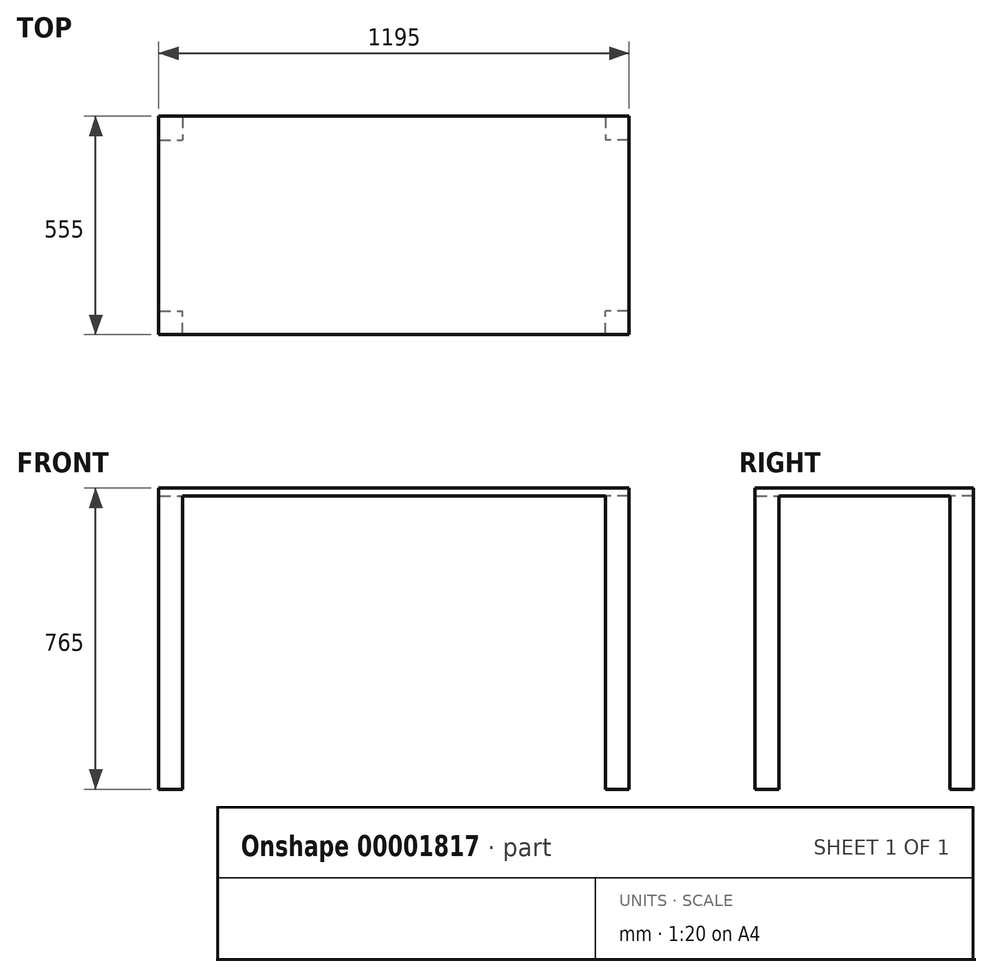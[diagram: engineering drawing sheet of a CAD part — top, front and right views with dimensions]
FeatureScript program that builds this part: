
annotation { "Feature Type Name" : "Feature", "Feature Type Description" : "" }
export const myFeature = defineFeature(function(context is Context, id is Id, definition is map)
    precondition{}
    {
        {
            var Q0;
            Q0=qCreatedBy(makeId("Top.planeOp"),FACE);
            var sketch = newSketch(context, id + "F0", { "sketchPlane" : qUnion([Q0])});
            skLineSegment(sketch, "E0.rect.bottom", {"start": v(597.5, -277.5) * mm, "end": v(-597.5, -277.5) * mm});
            skLineSegment(sketch, "E0.rect.top", {"start": v(597.5, 277.5) * mm, "end": v(-597.5, 277.5) * mm});
            skLineSegment(sketch, "E0.rect.left", {"start": v(597.5, -277.5) * mm, "end": v(597.5, 277.5) * mm});
            skLineSegment(sketch, "E0.rect.right", {"start": v(-597.5, -277.5) * mm, "end": v(-597.5, 277.5) * mm});
            skPoint(sketch, "E0.rect.middle", {"position": v(0, 0) * mm});
            skSolve(sketch);
        }
        {
            var Q0;
            Q0 = qSketchRegion(id + "F0", true);
            extrude(context, id + "F1", {"entities" : qUnion([Q0]), "depth" : 20 * mm});
        }
        {
            var Q0;
            Q0=makeQuery(id+"F1.opExtrude","CAP_FACE",FACE,{"disambiguationData":[OSD([sQuery(id+"F0.wireOp",EDGE,"E0.rect.bottom"),sQuery(id+"F0.wireOp",EDGE,"E0.rect.top"),sQuery(id+"F0.wireOp",EDGE,"E0.rect.left"),sQuery(id+"F0.wireOp",EDGE,"E0.rect.right")])],"isStart":true});
            var sketch = newSketch(context, id + "F2", { "sketchPlane" : qUnion([Q0])});
            skLineSegment(sketch, "E1", {"start": v(0, 277.5) * mm, "end": v(0, -277.5) * mm, "construction": true});
            skLineSegment(sketch, "E2.bottom", {"start": v(-597.5, 277.5) * mm, "end": v(-537.5, 277.5) * mm});
            skLineSegment(sketch, "E2.top", {"start": v(-597.5, 217.5) * mm, "end": v(-537.5, 217.5) * mm});
            skLineSegment(sketch, "E2.left", {"start": v(-597.5, 277.5) * mm, "end": v(-597.5, 217.5) * mm});
            skLineSegment(sketch, "E2.right", {"start": v(-537.5, 277.5) * mm, "end": v(-537.5, 217.5) * mm});
            skLineSegment(sketch, "E3.0.MirrorCS", {"start": v(597.5, 217.5) * mm, "end": v(537.5, 217.5) * mm});
            skLineSegment(sketch, "E4.0.MirrorCS", {"start": v(537.5, 277.5) * mm, "end": v(537.5, 217.5) * mm});
            skLineSegment(sketch, "E5.0.MirrorCS", {"start": v(597.5, 277.5) * mm, "end": v(537.5, 277.5) * mm});
            skLineSegment(sketch, "E6.2.MirrorCS", {"start": v(597.5, 277.5) * mm, "end": v(597.5, 217.5) * mm});
            skLineSegment(sketch, "E7", {"start": v(-597.5, 0) * mm, "end": v(597.5, 0) * mm, "construction": true});
            skLineSegment(sketch, "E8.0.MirrorCS", {"start": v(-597.5, -217.5) * mm, "end": v(-537.5, -217.5) * mm});
            skLineSegment(sketch, "E9.0.MirrorCS", {"start": v(-537.5, -277.5) * mm, "end": v(-537.5, -217.5) * mm});
            skLineSegment(sketch, "E10.0.MirrorCS", {"start": v(-597.5, -277.5) * mm, "end": v(-537.5, -277.5) * mm});
            skLineSegment(sketch, "E11.0.MirrorCS", {"start": v(-597.5, -277.5) * mm, "end": v(-597.5, -217.5) * mm});
            skLineSegment(sketch, "E12.0.MirrorCS", {"start": v(597.5, -217.5) * mm, "end": v(537.5, -217.5) * mm});
            skLineSegment(sketch, "E13.0.MirrorCS", {"start": v(537.5, -277.5) * mm, "end": v(537.5, -217.5) * mm});
            skLineSegment(sketch, "E14.0.MirrorCS", {"start": v(597.5, -277.5) * mm, "end": v(597.5, -217.5) * mm});
            skLineSegment(sketch, "E15.0.MirrorCS", {"start": v(597.5, -277.5) * mm, "end": v(537.5, -277.5) * mm});
            skSolve(sketch);
        }
        {
            var Q0;
            Q0 = qSketchRegion(id + "F2", true);
            extrude(context, id + "F3", {"entities" : qUnion([Q0]), "operationType" : NewBodyOperationType.ADD, "depth" : 745 * mm});
        }
    });
